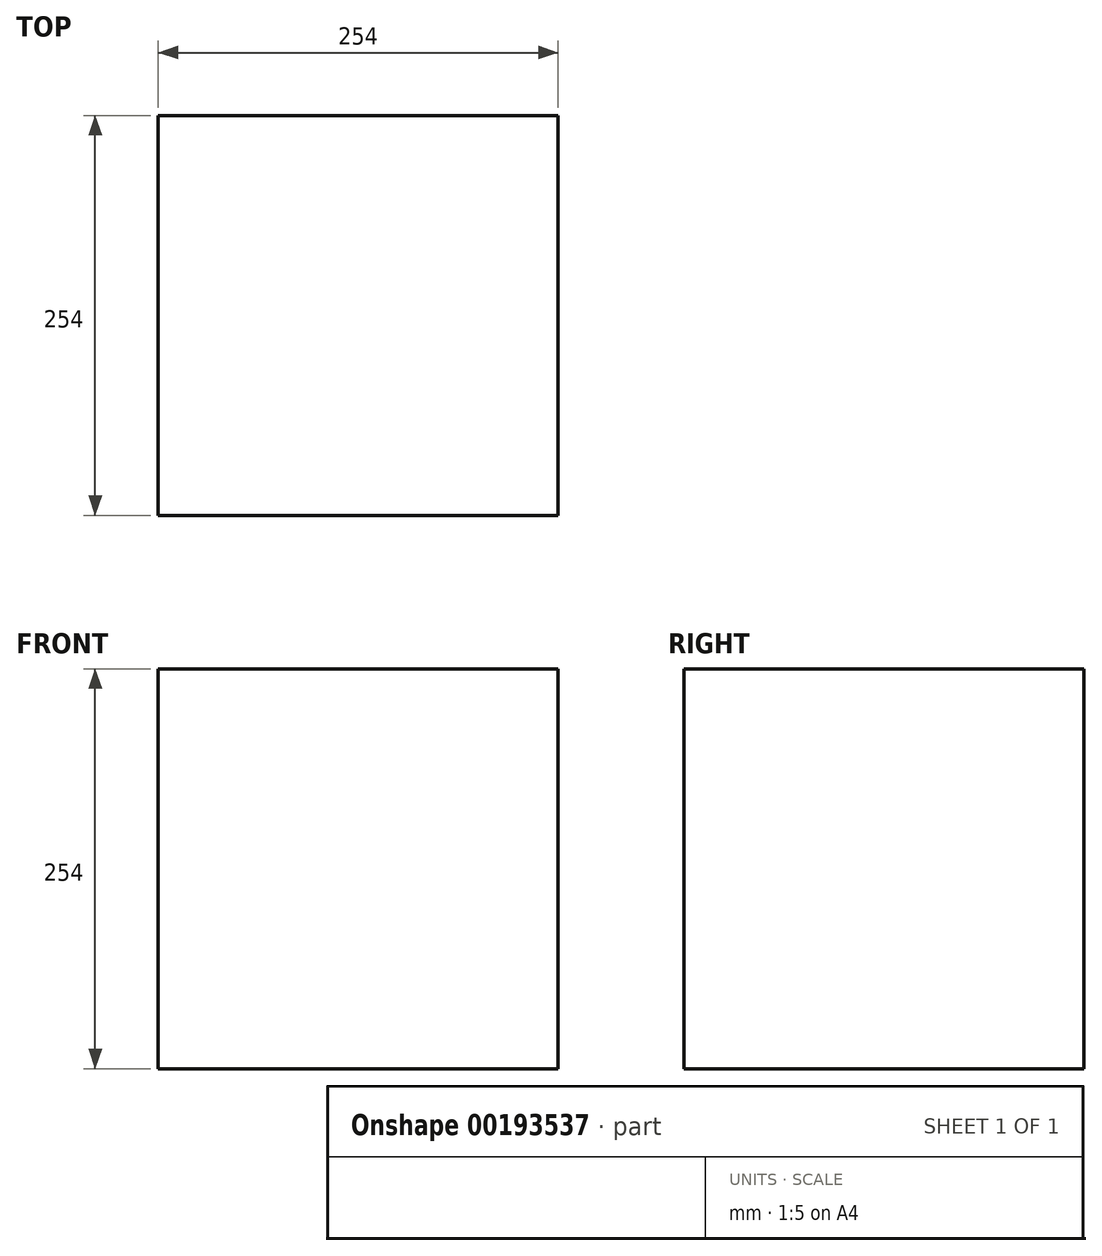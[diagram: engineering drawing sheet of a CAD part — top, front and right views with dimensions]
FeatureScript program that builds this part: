
annotation { "Feature Type Name" : "Feature", "Feature Type Description" : "" }
export const myFeature = defineFeature(function(context is Context, id is Id, definition is map)
    precondition{}
    {
        {
            var Q0;
            Q0=qCreatedBy(makeId("Top.planeOp"),FACE);
            var sketch = newSketch(context, id + "F0", { "sketchPlane" : qUnion([Q0])});
            skLineSegment(sketch, "E0.bottom", {"start": v(-131.54, 128.45) * mm, "end": v(122.46, 128.45) * mm});
            skLineSegment(sketch, "E0.top", {"start": v(-131.54, -125.55) * mm, "end": v(122.46, -125.55) * mm});
            skLineSegment(sketch, "E0.left", {"start": v(-131.54, 128.45) * mm, "end": v(-131.54, -125.55) * mm});
            skLineSegment(sketch, "E0.right", {"start": v(122.46, 128.45) * mm, "end": v(122.46, -125.55) * mm});
            skSolve(sketch);
        }
        {
            var Q0;
            Q0=makeQuery(id+"F0.imprint","IMPRINT",FACE,{"disambiguationData":[TD([[makeQuery(id+"F0.imprint","IMPRINT",EDGE,{"derivedFrom":sQuery(id+"F0.wireOp",EDGE,"E0.bottom")}),-1.0]])]});
            extrude(context, id + "F1", {"entities" : qUnion([Q0]), "depth" : 254 * mm});
        }
    });
